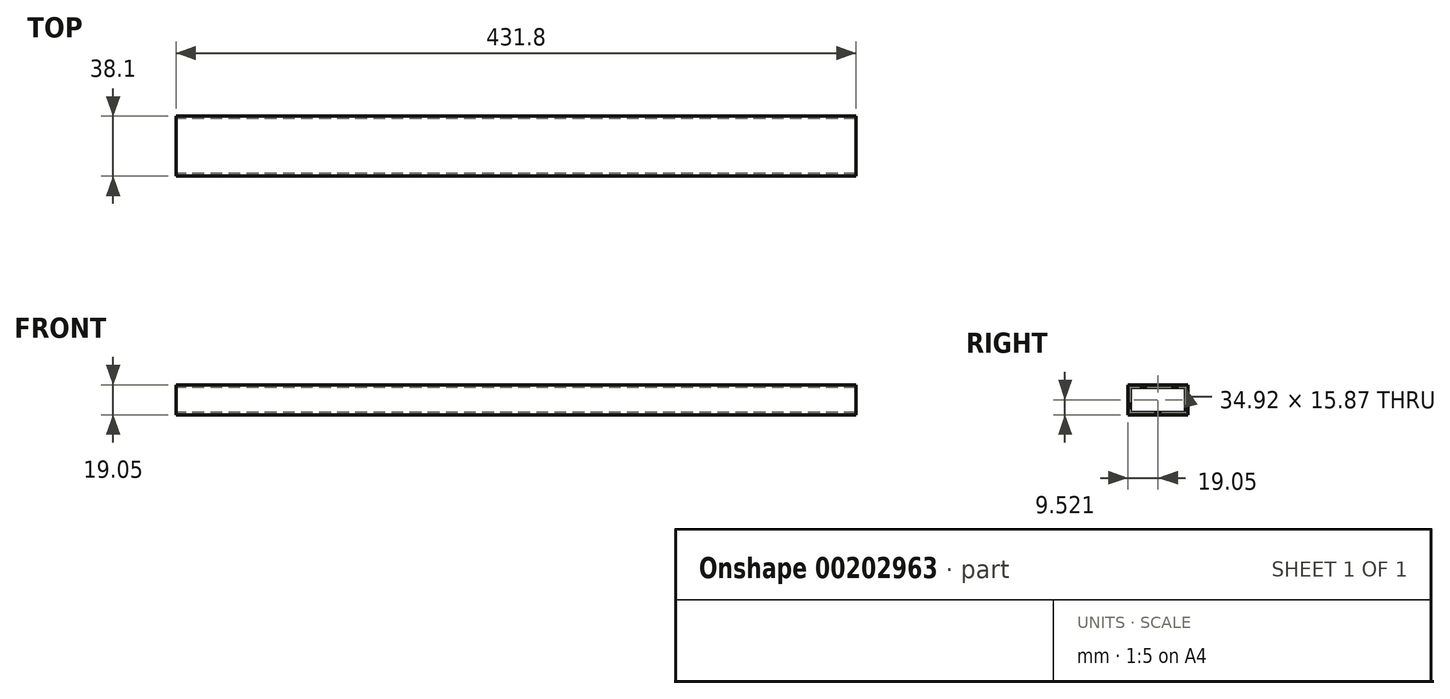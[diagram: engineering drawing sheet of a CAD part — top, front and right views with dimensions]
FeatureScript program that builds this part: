
annotation { "Feature Type Name" : "Feature", "Feature Type Description" : "" }
export const myFeature = defineFeature(function(context is Context, id is Id, definition is map)
    precondition{}
    {
        {
            var Q0;
            Q0=qCreatedBy(makeId("Right.planeOp"),FACE);
            var sketch = newSketch(context, id + "F0", { "sketchPlane" : qUnion([Q0])});
            skLineSegment(sketch, "E0.bottom", {"start": v(-17.46, -0.41) * mm, "end": v(17.46, -0.41) * mm});
            skLineSegment(sketch, "E0.top", {"start": v(-17.46, -16.29) * mm, "end": v(17.46, -16.29) * mm});
            skLineSegment(sketch, "E0.left", {"start": v(-17.46, -0.41) * mm, "end": v(-17.46, -16.29) * mm});
            skLineSegment(sketch, "E0.right", {"start": v(17.46, -0.41) * mm, "end": v(17.46, -16.29) * mm});
            skLineSegment(sketch, "E1.bottom", {"start": v(-19.05, 1.18) * mm, "end": v(19.05, 1.18) * mm});
            skLineSegment(sketch, "E1.top", {"start": v(-19.05, -17.87) * mm, "end": v(19.05, -17.87) * mm});
            skLineSegment(sketch, "E1.left", {"start": v(-19.05, 1.18) * mm, "end": v(-19.05, -17.87) * mm});
            skLineSegment(sketch, "E1.right", {"start": v(19.05, 1.18) * mm, "end": v(19.05, -17.87) * mm});
            skSolve(sketch);
        }
        {
            var Q0;
            Q0 = qSketchRegion(id + "F0", true);
            extrude(context, id + "F1", {"entities" : qUnion([Q0]), "depth" : 431.8 * mm});
        }
    });
